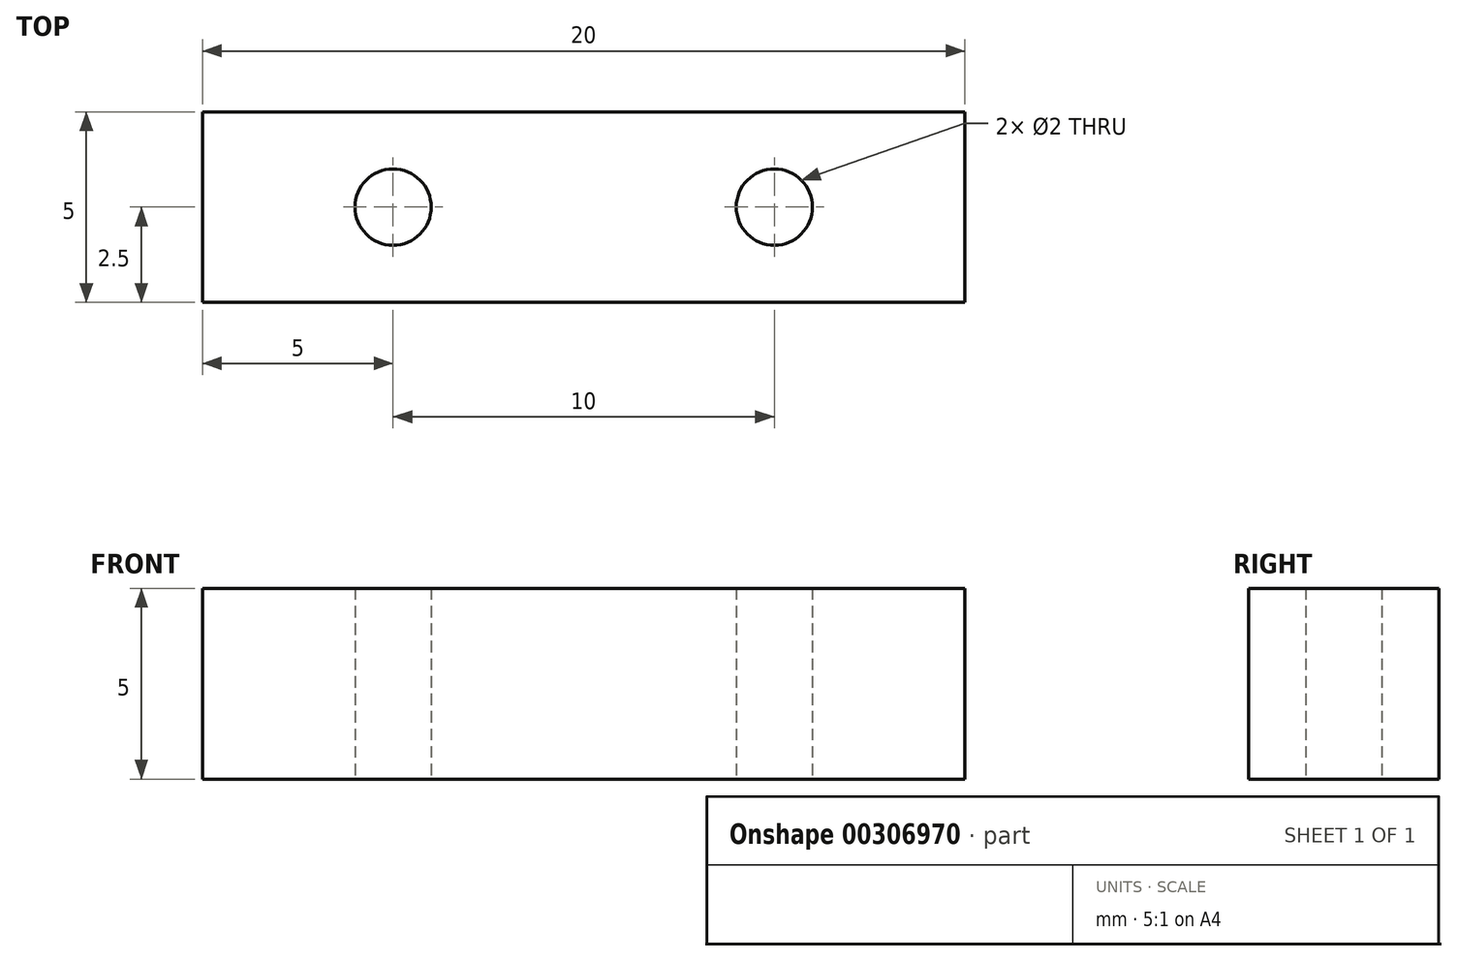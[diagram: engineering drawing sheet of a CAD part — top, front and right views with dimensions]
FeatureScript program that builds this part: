
annotation { "Feature Type Name" : "Feature", "Feature Type Description" : "" }
export const myFeature = defineFeature(function(context is Context, id is Id, definition is map)
    precondition{}
    {
        {
            var Q0;
            Q0=qCreatedBy(makeId("Front.planeOp"),FACE);
            var sketch = newSketch(context, id + "F0", { "sketchPlane" : qUnion([Q0])});
            skLineSegment(sketch, "E0.bottom", {"start": v(0, 0) * mm, "end": v(20, 0) * mm});
            skLineSegment(sketch, "E0.top", {"start": v(0, 5) * mm, "end": v(20, 5) * mm});
            skLineSegment(sketch, "E0.left", {"start": v(0, 0) * mm, "end": v(0, 5) * mm});
            skLineSegment(sketch, "E0.right", {"start": v(20, 0) * mm, "end": v(20, 5) * mm});
            skSolve(sketch);
        }
        {
            var Q0;
            Q0 = qSketchRegion(id + "F0", true);
            extrude(context, id + "F1", {"entities" : qUnion([Q0]), "depth" : 5 * mm});
        }
        {
            var Q0;
            Q0=makeQuery(id+"F1.opExtrude","SWEPT_FACE",FACE,{"disambiguationData":[OSD([sQuery(id+"F0.wireOp",EDGE,"E0.bottom")])]});
            var sketch = newSketch(context, id + "F2", { "sketchPlane" : qUnion([Q0])});
            skCircle(sketch, "E1", {"center": v(15, 2.5) * mm, "radius": 1 * mm});
            skPoint(sketch, "E1.centerSnap0", {"position": v(20, 2.5) * mm});
            skCircle(sketch, "E2", {"center": v(5, 2.5) * mm, "radius": 1 * mm});
            skPoint(sketch, "E2.centerSnap0", {"position": v(0, 2.5) * mm});
            skSolve(sketch);
        }
        {
            var Q0;
            Q0 = qSketchRegion(id + "F2", true);
            extrude(context, id + "F3", {"entities" : qUnion([Q0]), "operationType" : NewBodyOperationType.REMOVE, "oppositeDirection" : true, "depth" : 25 * mm});
        }
    });
